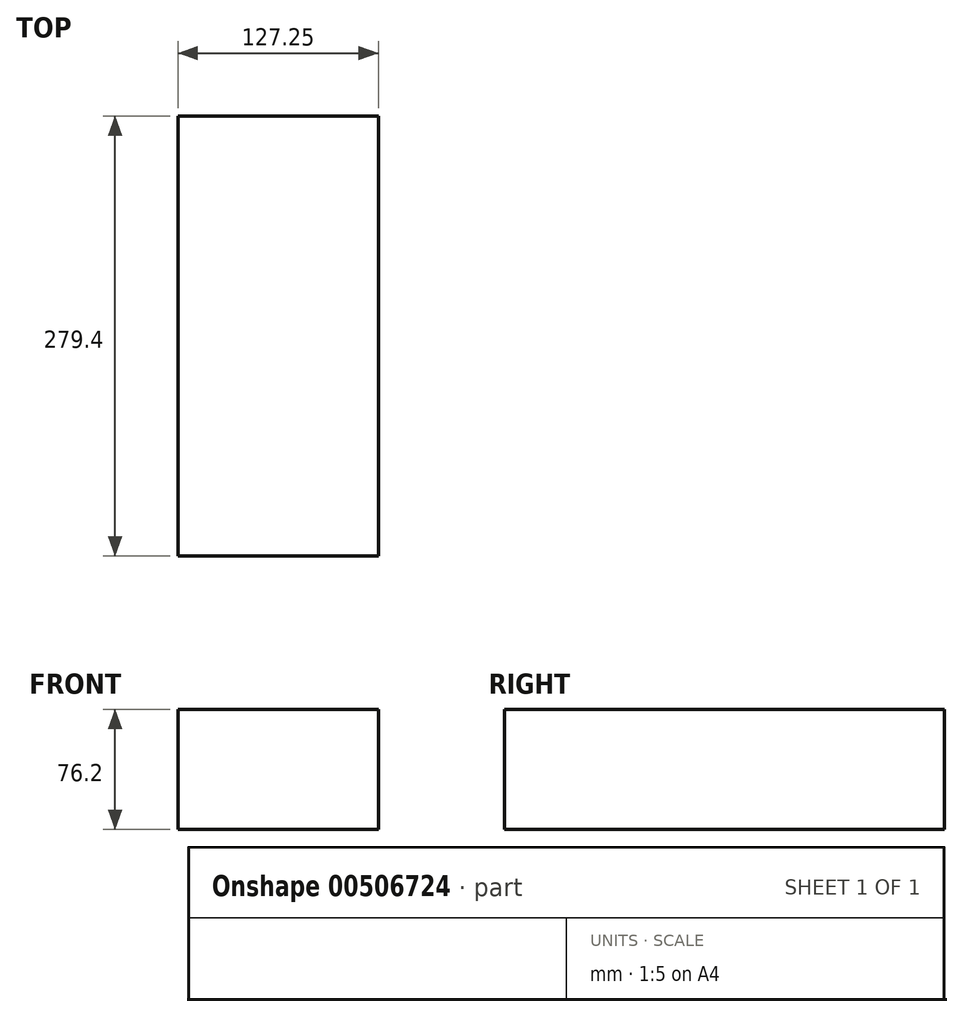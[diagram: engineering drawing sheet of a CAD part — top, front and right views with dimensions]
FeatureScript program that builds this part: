
annotation { "Feature Type Name" : "Feature", "Feature Type Description" : "" }
export const myFeature = defineFeature(function(context is Context, id is Id, definition is map)
    precondition{}
    {
        {
            var Q0;
            Q0=qCreatedBy(makeId("Front.planeOp"),FACE);
            var sketch = newSketch(context, id + "F0", { "sketchPlane" : qUnion([Q0])});
            skLineSegment(sketch, "E0.bottom", {"start": v(0, 0) * mm, "end": v(127.25, 0) * mm});
            skLineSegment(sketch, "E0.top", {"start": v(0, 76.2) * mm, "end": v(127.25, 76.2) * mm});
            skLineSegment(sketch, "E0.left", {"start": v(0, 0) * mm, "end": v(0, 76.2) * mm});
            skLineSegment(sketch, "E0.right", {"start": v(127.25, 0) * mm, "end": v(127.25, 76.2) * mm});
            skSolve(sketch);
        }
        {
            var Q0;
            Q0 = qSketchRegion(id + "F0", true);
            extrude(context, id + "F1", {"entities" : qUnion([Q0]), "depth" : 279.4 * mm, "offsetDistance" : 25 * mm});
        }
    });
